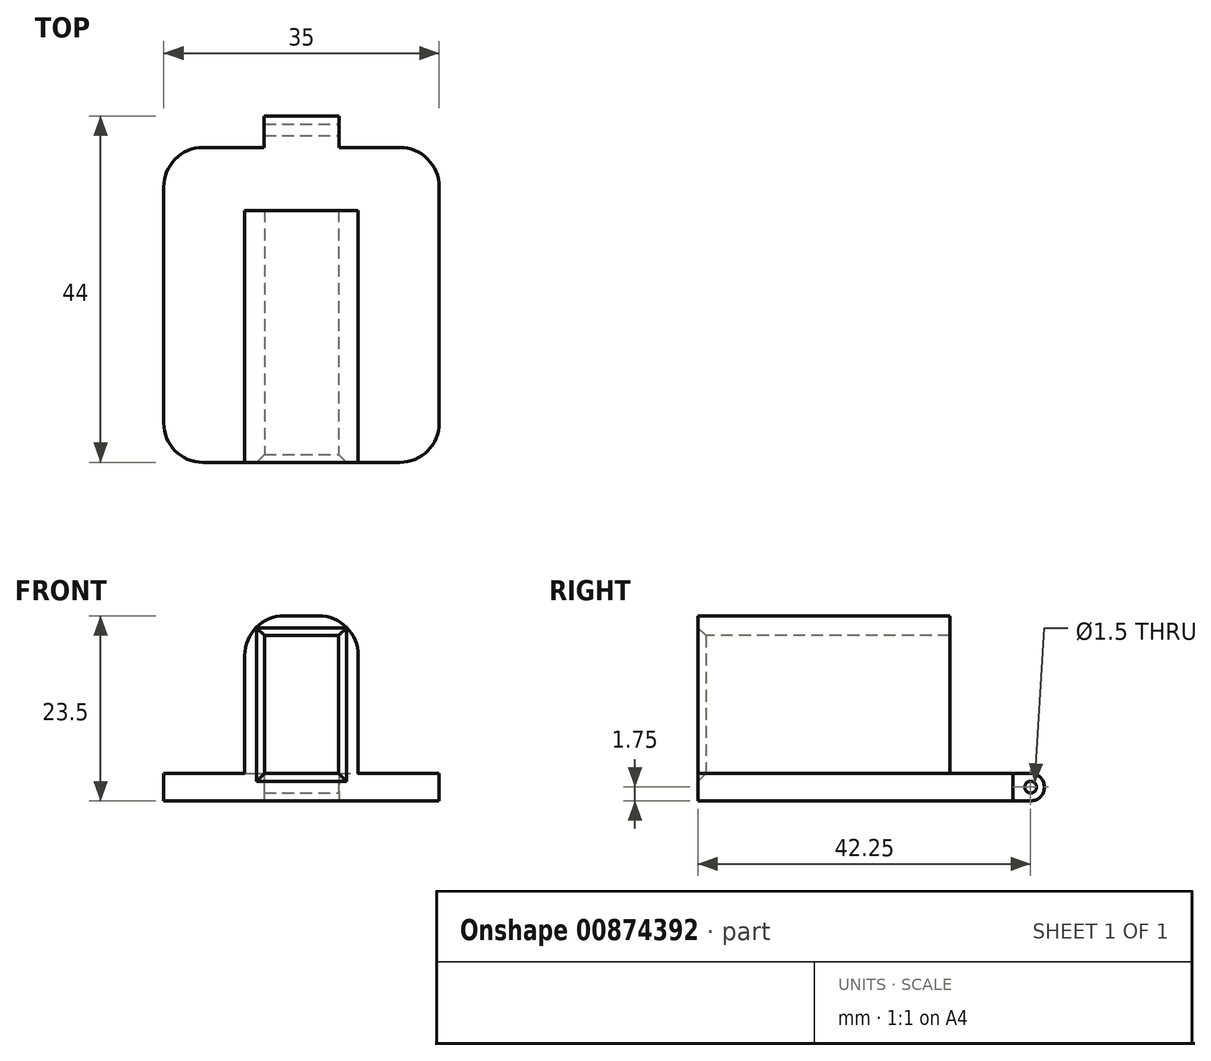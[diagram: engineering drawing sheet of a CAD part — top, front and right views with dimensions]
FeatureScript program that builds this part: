
annotation { "Feature Type Name" : "Feature", "Feature Type Description" : "" }
export const myFeature = defineFeature(function(context is Context, id is Id, definition is map)
    precondition{}
    {
        {
            var Q0;
            Q0=qCreatedBy(makeId("Top.planeOp"),FACE);
            var sketch = newSketch(context, id + "F0", { "sketchPlane" : qUnion([Q0])});
            skLineSegment(sketch, "E0.bottom", {"start": v(0, 0) * mm, "end": v(35, 0) * mm});
            skLineSegment(sketch, "E0.top", {"start": v(0, 40) * mm, "end": v(35, 40) * mm});
            skLineSegment(sketch, "E0.left", {"start": v(0, 0) * mm, "end": v(0, 40) * mm});
            skLineSegment(sketch, "E0.right", {"start": v(35, 0) * mm, "end": v(35, 40) * mm});
            skLineSegment(sketch, "E1.bottom", {"start": v(22.25, 40) * mm, "end": v(12.75, 40) * mm});
            skLineSegment(sketch, "E1.top", {"start": v(22.25, 44) * mm, "end": v(12.75, 44) * mm});
            skLineSegment(sketch, "E1.left", {"start": v(22.25, 40) * mm, "end": v(22.25, 44) * mm});
            skLineSegment(sketch, "E1.right", {"start": v(12.75, 40) * mm, "end": v(12.75, 44) * mm});
            skSolve(sketch);
        }
        {
            var Q0;
            Q0 = qSketchRegion(id + "F0", true);
            extrude(context, id + "F1", {"entities" : qUnion([Q0]), "depth" : 3.5 * mm, "offsetDistance" : 25 * mm});
        }
        {
            var Q0;
            Q0=makeQuery(id+"F1.opExtrude","CAP_EDGE",EDGE,{"disambiguationData":[OSD([sQuery(id+"F0.wireOp",EDGE,"E1.top")])],"isStart":false});
            var Q1;
            Q1=makeQuery(id+"F1.opExtrude","CAP_EDGE",EDGE,{"disambiguationData":[OSD([sQuery(id+"F0.wireOp",EDGE,"E1.top")])],"isStart":true});
            fillet(context, id + "F2", {"entities" : qUnion([Q0, Q1]), "radius" : 1.75 * mm, "tangentPropagation" : true, "allowEdgeOverflow" : false});
        }
        {
            var Q0;
            Q0=makeQuery(id+"F1.opExtrude","SWEPT_FACE",FACE,{"disambiguationData":[OSD([sQuery(id+"F0.wireOp",EDGE,"E1.left")])]});
            var sketch = newSketch(context, id + "F3", { "sketchPlane" : qUnion([Q0])});
            skCircle(sketch, "E2", {"center": v(42.25, 1.75) * mm, "radius": 0.75 * mm});
            skSolve(sketch);
        }
        {
            var Q0;
            Q0 = qSketchRegion(id + "F3", true);
            extrude(context, id + "F4", {"entities" : qUnion([Q0]), "operationType" : NewBodyOperationType.REMOVE, "oppositeDirection" : true, "depth" : 10 * mm, "offsetDistance" : 25 * mm});
        }
        {
            var Q0;
            Q0=makeQuery(id+"F1.opExtrude","CAP_FACE",FACE,{"disambiguationData":[OSD([sQuery(id+"F0.wireOp",EDGE,"E0.bottom"),sQuery(id+"F0.wireOp",EDGE,"E0.top"),sQuery(id+"F0.wireOp",EDGE,"E0.left"),sQuery(id+"F0.wireOp",EDGE,"E0.right"),sQuery(id+"F0.wireOp",EDGE,"E1.top"),sQuery(id+"F0.wireOp",EDGE,"E1.left"),sQuery(id+"F0.wireOp",EDGE,"E1.right")])],"isStart":false});
            var sketch = newSketch(context, id + "F5", { "sketchPlane" : qUnion([Q0])});
            skLineSegment(sketch, "E3.bottom", {"start": v(10.3, 32) * mm, "end": v(12.8, 32) * mm});
            skLineSegment(sketch, "E3.top", {"start": v(10.3, 0) * mm, "end": v(12.8, 0) * mm});
            skLineSegment(sketch, "E3.left", {"start": v(10.3, 32) * mm, "end": v(10.3, 0) * mm});
            skLineSegment(sketch, "E3.right", {"start": v(12.8, 32) * mm, "end": v(12.8, 0) * mm});
            skLineSegment(sketch, "E4.bottom", {"start": v(22.2, 32) * mm, "end": v(24.7, 32) * mm});
            skLineSegment(sketch, "E4.top", {"start": v(22.2, 0) * mm, "end": v(24.7, 0) * mm});
            skLineSegment(sketch, "E4.left", {"start": v(22.2, 32) * mm, "end": v(22.2, 0) * mm});
            skLineSegment(sketch, "E4.right", {"start": v(24.7, 32) * mm, "end": v(24.7, 0) * mm});
            skSolve(sketch);
        }
        {
            var Q0;
            Q0 = qSketchRegion(id + "F5", true);
            extrude(context, id + "F6", {"entities" : qUnion([Q0]), "operationType" : NewBodyOperationType.ADD, "depth" : 17.5 * mm, "offsetDistance" : 25 * mm});
        }
        {
            var Q0;
            Q0=makeQuery(id+"F6.opExtrude","CAP_FACE",FACE,{"disambiguationData":[OSD([sQuery(id+"F5.wireOp",EDGE,"E3.bottom"),sQuery(id+"F5.wireOp",EDGE,"E3.top"),sQuery(id+"F5.wireOp",EDGE,"E3.left"),sQuery(id+"F5.wireOp",EDGE,"E3.right")])],"isStart":false});
            var sketch = newSketch(context, id + "F7", { "sketchPlane" : qUnion([Q0])});
            skLineSegment(sketch, "E5.bottom", {"start": v(10.3, 32) * mm, "end": v(24.7, 32) * mm});
            skLineSegment(sketch, "E5.top", {"start": v(10.3, 0) * mm, "end": v(24.7, 0) * mm});
            skLineSegment(sketch, "E5.left", {"start": v(10.3, 32) * mm, "end": v(10.3, 0) * mm});
            skLineSegment(sketch, "E5.right", {"start": v(24.7, 32) * mm, "end": v(24.7, 0) * mm});
            skSolve(sketch);
        }
        {
            var Q0;
            Q0 = qSketchRegion(id + "F7", true);
            extrude(context, id + "F8", {"entities" : qUnion([Q0]), "operationType" : NewBodyOperationType.ADD, "depth" : 2.5 * mm, "offsetDistance" : 25 * mm});
        }
        {
            var Q0;
            Q0=makeQuery(id+"F8.opExtrude","CAP_EDGE",EDGE,{"disambiguationData":[OSD([sQuery(id+"F7.wireOp",EDGE,"E5.right")])],"isStart":false});
            var Q1;
            Q1=makeQuery(id+"F8.opExtrude","CAP_EDGE",EDGE,{"disambiguationData":[OSD([sQuery(id+"F7.wireOp",EDGE,"E5.left")])],"isStart":false});
            var Q2;
            Q2=makeQuery(id+"F6.opExtrude","CAP_EDGE",EDGE,{"disambiguationData":[OSD([sQuery(id+"F5.wireOp",EDGE,"E4.right")])],"isStart":true});
            var Q3;
            Q3=makeQuery(id+"F6.opExtrude","CAP_EDGE",EDGE,{"disambiguationData":[OSD([sQuery(id+"F5.wireOp",EDGE,"E3.left")])],"isStart":true});
            var Q4;
            Q4=makeQuery(id+"F1.opExtrude","SWEPT_EDGE",EDGE,{"disambiguationData":[OSD([sQuery(id+"F0.wireOp",EDGE,"E0.top"),sQuery(id+"F0.wireOp",EDGE,"E0.right")])]});
            var Q5;
            Q5=makeQuery(id+"F1.opExtrude","SWEPT_EDGE",EDGE,{"disambiguationData":[OSD([sQuery(id+"F0.wireOp",EDGE,"E0.top"),sQuery(id+"F0.wireOp",EDGE,"E0.left")])]});
            var Q6;
            Q6=makeQuery(id+"F1.opExtrude","SWEPT_EDGE",EDGE,{"disambiguationData":[OSD([sQuery(id+"F0.wireOp",EDGE,"E0.bottom"),sQuery(id+"F0.wireOp",EDGE,"E0.left")])]});
            var Q7;
            Q7=makeQuery(id+"F1.opExtrude","SWEPT_EDGE",EDGE,{"disambiguationData":[OSD([sQuery(id+"F0.wireOp",EDGE,"E0.bottom"),sQuery(id+"F0.wireOp",EDGE,"E0.right")])]});
            fillet(context, id + "F9", {"entities" : qUnion([Q0, Q1, Q2, Q3, Q4, Q5, Q6, Q7]), "radius" : 5 * mm, "tangentPropagation" : true, "allowEdgeOverflow" : false});
        }
        {
            var Q0;
            Q0=makeQuery(id+"F6.opExtrude","SWEPT_EDGE",EDGE,{"disambiguationData":[OSD([sQuery(id+"F0.wireOp",EDGE,"E0.bottom"),sQuery(id+"F5.wireOp",EDGE,"E3.top"),sQuery(id+"F5.wireOp",EDGE,"E3.right")])]});
            var Q1;
            {var subQ0=sQuery(id+"F0.wireOp",EDGE,"E0.bottom");Q1=makeQuery(id+"F6.boolean.opBoolean","SPLIT",EDGE,{"disambiguationData":[TD([makeQuery(id+"F6.opExtrude","SWEPT_FACE",FACE,{"disambiguationData":[OSD([sQuery(id+"F5.wireOp",EDGE,"E3.right")])]})])],"derivedFrom":makeQuery(id+"F1.opExtrude","CAP_EDGE",EDGE,{"disambiguationData":[OSD([subQ0])],"isStart":false})});}
            var Q2;
            Q2=makeQuery(id+"F6.opExtrude","SWEPT_EDGE",EDGE,{"disambiguationData":[OSD([sQuery(id+"F0.wireOp",EDGE,"E0.bottom"),sQuery(id+"F5.wireOp",EDGE,"E4.top"),sQuery(id+"F5.wireOp",EDGE,"E4.left")])]});
            var Q3;
            Q3=makeQuery(id+"F8.opExtrude","CAP_EDGE",EDGE,{"disambiguationData":[OSD([sQuery(id+"F7.wireOp",EDGE,"E5.top")])],"isStart":true});
            chamfer(context, id + "F10", {"entities" : qUnion([Q0, Q1, Q2, Q3]), "width" : 1 * mm, "tangentPropagation" : true});
        }
    });
